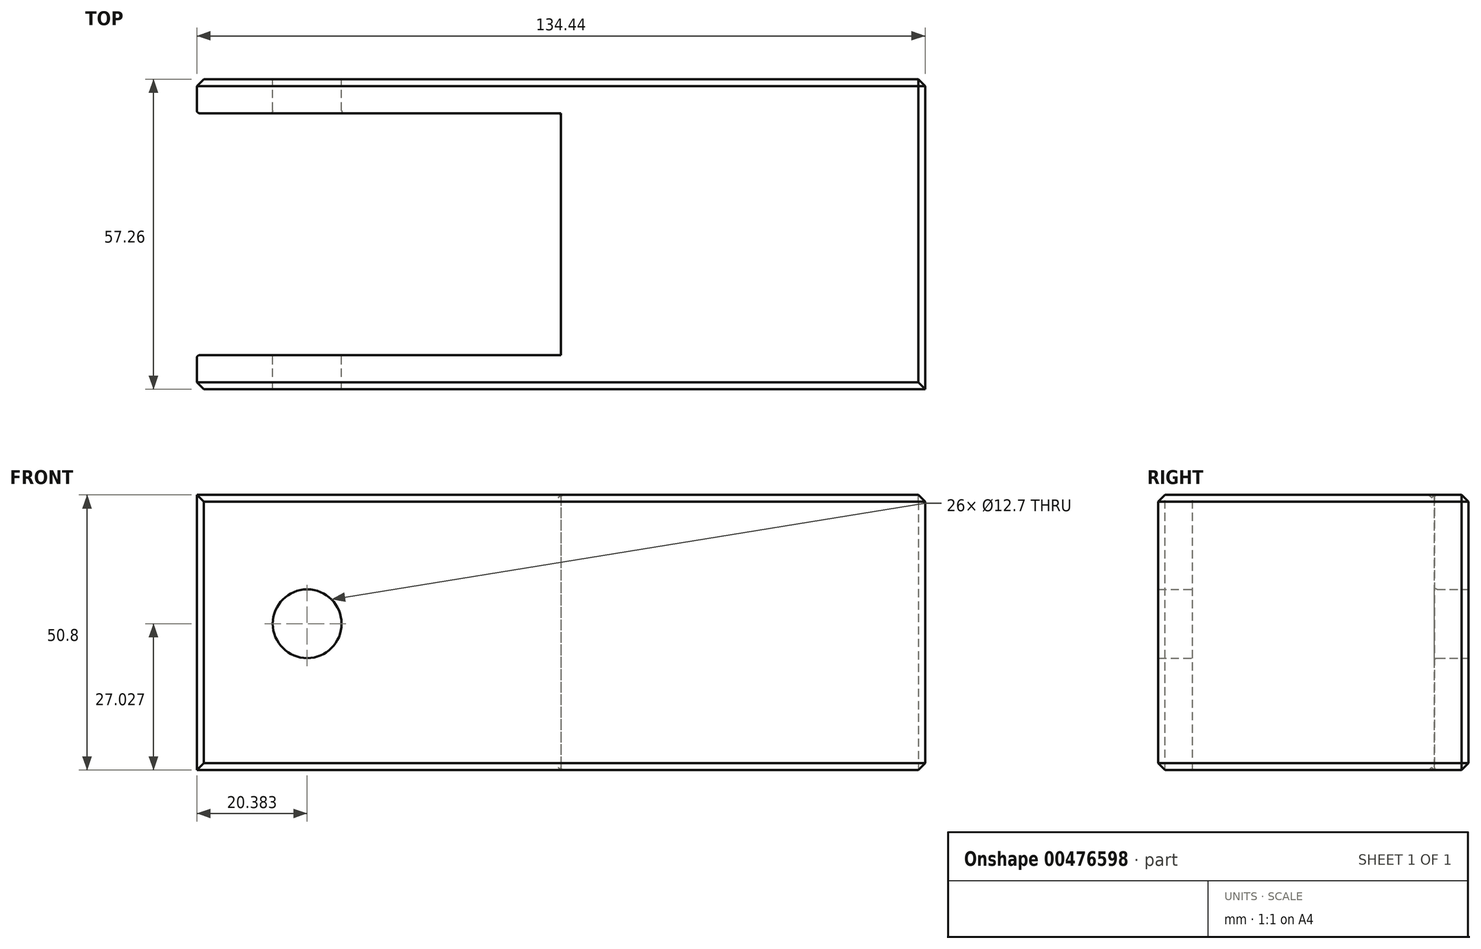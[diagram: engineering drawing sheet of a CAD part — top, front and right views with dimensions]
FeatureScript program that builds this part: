
annotation { "Feature Type Name" : "Feature", "Feature Type Description" : "" }
export const myFeature = defineFeature(function(context is Context, id is Id, definition is map)
    precondition{}
    {
        {
            var Q0;
            Q0=qCreatedBy(makeId("Top.planeOp"),FACE);
            var sketch = newSketch(context, id + "F0", { "sketchPlane" : qUnion([Q0])});
            skLineSegment(sketch, "E0.bottom", {"start": v(67.22, -28.63) * mm, "end": v(-67.22, -28.63) * mm});
            skLineSegment(sketch, "E0.top", {"start": v(67.22, 28.63) * mm, "end": v(-67.22, 28.63) * mm});
            skLineSegment(sketch, "E0.left", {"start": v(67.22, -28.63) * mm, "end": v(67.22, 28.63) * mm});
            skLineSegment(sketch, "E0.right", {"start": v(-67.22, -28.63) * mm, "end": v(-67.22, 28.63) * mm});
            skPoint(sketch, "E0.middle", {"position": v(0, 0) * mm});
            skSolve(sketch);
        }
        {
            var Q0;
            Q0 = qSketchRegion(id + "F0", true);
            extrude(context, id + "F1", {"entities" : qUnion([Q0]), "depth" : 50.8 * mm});
        }
        {
            var Q0;
            Q0=qCreatedBy(makeId("Top.planeOp"),FACE);
            var sketch = newSketch(context, id + "F2", { "sketchPlane" : qUnion([Q0])});
            skLineSegment(sketch, "E1.bottom", {"start": v(0, -22.34) * mm, "end": v(-77.68, -22.34) * mm});
            skLineSegment(sketch, "E1.top", {"start": v(0, 22.34) * mm, "end": v(-77.68, 22.34) * mm});
            skLineSegment(sketch, "E1.left", {"start": v(0, -22.34) * mm, "end": v(0, 22.34) * mm});
            skLineSegment(sketch, "E1.right", {"start": v(-77.68, -22.34) * mm, "end": v(-77.68, 22.34) * mm});
            skPoint(sketch, "E1.middle", {"position": v(-38.84, 0) * mm});
            skSolve(sketch);
        }
        {
            var Q0;
            Q0 = qSketchRegion(id + "F2", true);
            extrude(context, id + "F3", {"entities" : qUnion([Q0]), "operationType" : NewBodyOperationType.REMOVE, "depth" : 50.8 * mm});
        }
        {
            var Q0;
            Q0=makeQuery(id+"F1.opExtrude","SWEPT_FACE",FACE,{"disambiguationData":[OSD([sQuery(id+"F0.wireOp",EDGE,"E0.top")])]});
            var sketch = newSketch(context, id + "F4", { "sketchPlane" : qUnion([Q0])});
            skPoint(sketch, "E2", {"position": v(46.84, 27.03) * mm});
            skSolve(sketch);
        }
        {
            var Q0;
            Q0=sQuery(id+"F4.wireOp",VERTEX,"E2");
            var Q1;
            Q1=makeQuery(id+"F1.opExtrude","SWEPT_BODY",BODY,{"disambiguationData":[OSD([sQuery(id+"F0.wireOp",EDGE,"E0.bottom"),sQuery(id+"F0.wireOp",EDGE,"E0.top"),sQuery(id+"F0.wireOp",EDGE,"E0.left"),sQuery(id+"F0.wireOp",EDGE,"E0.right")])]});
            hole(context, id + "F5", {"style" : HoleStyle.SIMPLE, "endStyle" : HoleEndStyle.THROUGH, "standardTappedOrClearance" : lookupTablePath({ "standard" : "Custom", "fit" : "Normal", "engagement" : "75%", "pitch" : "16 tpi", "size" : "3/8", "type" : "Clearance" }), "standardBlindInLast" : lookupTablePath({ "fit" : "Free", "standard" : "Custom", "engagement" : "75%", "pitch" : "16 tpi", "size" : "3/8", "type" : "Clearance" }), "holeDiameter" : 12.7 * mm, "showTappedDepth" : true, "isTappedThrough" : true, "tappedDepth" : 12.7 * mm, "tapClearance" : 3, "locations" : qUnion([Q0]), "scope" : qUnion([Q1])});
        }
        {
            var Q0;
            Q0=makeQuery(id+"F5.hole-0.boolean.opBoolean","COPY",EDGE,{"derivedFrom":makeQuery(id+"F5.hole-0.opRevolve","SWEPT_EDGE",EDGE,{"disambiguationData":[OSD([sQuery(id+"F5.hole-0.sketch.wireOp",EDGE,"core_line_2"),sQuery(id+"F5.hole-0.sketch.wireOp",EDGE,"core_line_3")])]})});
            var Q1;
            Q1=makeQuery(id+"F5.hole-0.boolean.opBoolean","INTERSECT",EDGE,{"derivedFrom":[makeQuery(id+"F3.boolean.opBoolean","COPY",FACE,{"derivedFrom":makeQuery(id+"F3.opExtrude","SWEPT_FACE",FACE,{"disambiguationData":[OSD([sQuery(id+"F2.wireOp",EDGE,"E1.bottom")])]})}),makeQuery(id+"F5.hole-0.opRevolve","SWEPT_FACE",FACE,{"disambiguationData":[OSD([sQuery(id+"F5.hole-0.sketch.wireOp",EDGE,"core_line_2")])]})]});
            var Q2;
            Q2=makeQuery(id+"F3.boolean.opBoolean","COPY",FACE,{"derivedFrom":makeQuery(id+"F3.opExtrude","SWEPT_FACE",FACE,{"disambiguationData":[OSD([sQuery(id+"F2.wireOp",EDGE,"E1.top")])]})});
            var Q3;
            Q3=makeQuery(id+"F5.hole-0.boolean.opBoolean","INTERSECT",EDGE,{"derivedFrom":[makeQuery(id+"F1.opExtrude","SWEPT_FACE",FACE,{"disambiguationData":[OSD([sQuery(id+"F0.wireOp",EDGE,"E0.bottom")])]}),makeQuery(id+"F5.hole-0.opRevolve","SWEPT_FACE",FACE,{"disambiguationData":[OSD([sQuery(id+"F5.hole-0.sketch.wireOp",EDGE,"core_line_2")])]})]});
            var Q4;
            Q4=makeQuery(id+"F3.boolean.opBoolean","INTERSECT",EDGE,{"derivedFrom":[makeQuery(id+"F1.opExtrude","SWEPT_FACE",FACE,{"disambiguationData":[OSD([sQuery(id+"F0.wireOp",EDGE,"E0.right")])]}),makeQuery(id+"F3.opExtrude","SWEPT_FACE",FACE,{"disambiguationData":[OSD([sQuery(id+"F2.wireOp",EDGE,"E1.bottom")])]})]});
            var Q5;
            Q5=makeQuery(id+"F3.boolean.opBoolean","COPY",EDGE,{"derivedFrom":makeQuery(id+"F3.opExtrude","CAP_EDGE",EDGE,{"disambiguationData":[OSD([sQuery(id+"F2.wireOp",EDGE,"E1.bottom")])],"isStart":true})});
            var Q6;
            Q6=makeQuery(id+"F3.boolean.opBoolean","COPY",EDGE,{"derivedFrom":makeQuery(id+"F3.opExtrude","CAP_EDGE",EDGE,{"disambiguationData":[OSD([sQuery(id+"F2.wireOp",EDGE,"E1.bottom")])],"isStart":false})});
            fillet(context, id + "F6", {"entities" : qUnion([Q0, Q1, Q2, Q3, Q4, Q5, Q6]), "radius" : 0.5 * mm, "tangentPropagation" : true, "allowEdgeOverflow" : false});
        }
        {
            var Q0;
            Q0=makeQuery(id+"F1.opExtrude","CAP_EDGE",EDGE,{"disambiguationData":[OSD([sQuery(id+"F0.wireOp",EDGE,"E0.top")])],"isStart":false});
            var Q1;
            Q1=makeQuery(id+"F1.opExtrude","SWEPT_EDGE",EDGE,{"disambiguationData":[OSD([sQuery(id+"F0.wireOp",EDGE,"E0.top"),sQuery(id+"F0.wireOp",EDGE,"E0.right")])]});
            var Q2;
            Q2=makeQuery(id+"F1.opExtrude","CAP_EDGE",EDGE,{"disambiguationData":[OSD([sQuery(id+"F0.wireOp",EDGE,"E0.top")])],"isStart":true});
            var Q3;
            Q3=makeQuery(id+"F1.opExtrude","SWEPT_EDGE",EDGE,{"disambiguationData":[OSD([sQuery(id+"F0.wireOp",EDGE,"E0.top"),sQuery(id+"F0.wireOp",EDGE,"E0.left")])]});
            var Q4;
            Q4=makeQuery(id+"F1.opExtrude","CAP_EDGE",EDGE,{"disambiguationData":[OSD([sQuery(id+"F0.wireOp",EDGE,"E0.left")])],"isStart":false});
            var Q5;
            Q5=makeQuery(id+"F1.opExtrude","CAP_EDGE",EDGE,{"disambiguationData":[OSD([sQuery(id+"F0.wireOp",EDGE,"E0.left")])],"isStart":true});
            var Q6;
            Q6=makeQuery(id+"F1.opExtrude","CAP_EDGE",EDGE,{"disambiguationData":[OSD([sQuery(id+"F0.wireOp",EDGE,"E0.bottom")])],"isStart":true});
            var Q7;
            Q7=makeQuery(id+"F1.opExtrude","CAP_EDGE",EDGE,{"disambiguationData":[OSD([sQuery(id+"F0.wireOp",EDGE,"E0.bottom")])],"isStart":false});
            var Q8;
            Q8=makeQuery(id+"F1.opExtrude","SWEPT_EDGE",EDGE,{"disambiguationData":[OSD([sQuery(id+"F0.wireOp",EDGE,"E0.bottom"),sQuery(id+"F0.wireOp",EDGE,"E0.right")])]});
            chamfer(context, id + "F7", {"entities" : qUnion([Q0, Q1, Q2, Q3, Q4, Q5, Q6, Q7, Q8]), "width" : 1.27 * mm, "tangentPropagation" : true});
        }
    });
